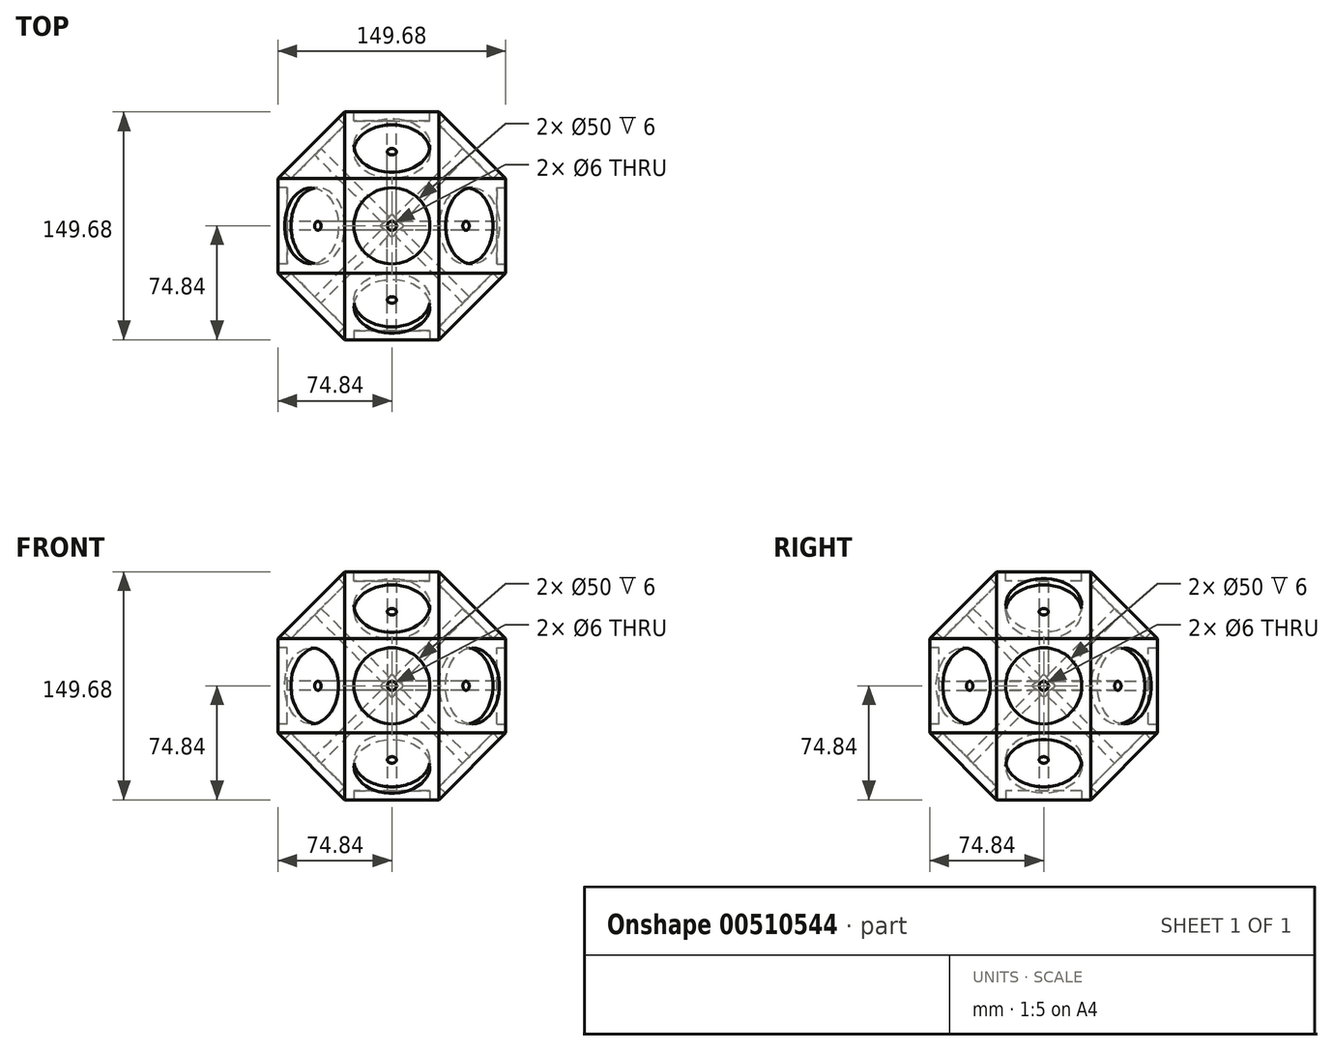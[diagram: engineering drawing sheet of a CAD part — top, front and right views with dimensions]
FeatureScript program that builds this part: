
annotation { "Feature Type Name" : "Feature", "Feature Type Description" : "" }
export const myFeature = defineFeature(function(context is Context, id is Id, definition is map)
    precondition{}
    {
        {
            var Q0;
            Q0=qCreatedBy(makeId("Front.planeOp"),FACE);
            var sketch = newSketch(context, id + "F0", { "sketchPlane" : qUnion([Q0])});
            skLineSegment(sketch, "E0.bottom", {"start": v(0, 0) * mm, "end": v(74.84, 0) * mm, "construction": true});
            skLineSegment(sketch, "E0.top", {"start": v(0, 31) * mm, "end": v(74.84, 31) * mm});
            skLineSegment(sketch, "E0.left", {"start": v(0, 0) * mm, "end": v(0, 31) * mm});
            skLineSegment(sketch, "E0.right", {"start": v(74.84, 0) * mm, "end": v(74.84, 31) * mm});
            skLineSegment(sketch, "E1.top", {"start": v(0, -31) * mm, "end": v(74.84, -31) * mm});
            skLineSegment(sketch, "E1.left", {"start": v(0, 0) * mm, "end": v(0, -31) * mm});
            skLineSegment(sketch, "E1.right", {"start": v(74.84, 0) * mm, "end": v(74.84, -31) * mm});
            skLineSegment(sketch, "E2.bottom", {"start": v(0, 31) * mm, "end": v(-31, 31) * mm, "construction": true});
            skLineSegment(sketch, "E2.top", {"start": v(0, -31) * mm, "end": v(-31, -31) * mm, "construction": true});
            skLineSegment(sketch, "E2.left", {"start": v(0, 31) * mm, "end": v(0, -31) * mm, "construction": true});
            skLineSegment(sketch, "E2.right", {"start": v(-31, 31) * mm, "end": v(-31, -31) * mm, "construction": true});
            skLineSegment(sketch, "E3.bottom", {"start": v(0, 0) * mm, "end": v(31, 0) * mm, "construction": true});
            skLineSegment(sketch, "E3.top", {"start": v(0, 74.84) * mm, "end": v(31, 74.84) * mm, "construction": true});
            skLineSegment(sketch, "E3.left", {"start": v(0, 0) * mm, "end": v(0, 74.84) * mm, "construction": true});
            skLineSegment(sketch, "E3.right", {"start": v(31, 0) * mm, "end": v(31, 74.84) * mm, "construction": true});
            skLineSegment(sketch, "E4.bottom", {"start": v(0, 0) * mm, "end": v(-31, 0) * mm, "construction": true});
            skLineSegment(sketch, "E4.top", {"start": v(0, 74.84) * mm, "end": v(-31, 74.84) * mm, "construction": true});
            skLineSegment(sketch, "E4.right", {"start": v(-31, 0) * mm, "end": v(-31, 74.84) * mm, "construction": true});
            skLineSegment(sketch, "E5", {"start": v(31, 74.84) * mm, "end": v(74.84, 31) * mm, "construction": true});
            skSolve(sketch);
        }
        {
            var Q0;
            Q0=makeQuery(id+"F0.imprint","IMPRINT",FACE,{"disambiguationData":[TD([[makeQuery(id+"F0.imprint","IMPRINT",EDGE,{"derivedFrom":sQuery(id+"F0.wireOp",EDGE,"E0.top")}),-1.0]])]});
            extrude(context, id + "F1", {"entities" : qUnion([Q0]), "depth" : 31 * mm, "hasSecondDirection" : true, "secondDirectionOppositeDirection" : true, "secondDirectionDepth" : 31 * mm});
        }
        {
            var Q0;
            Q0=makeQuery(id+"F1.opExtrude","SWEPT_FACE",FACE,{"disambiguationData":[OSD([sQuery(id+"F0.wireOp",EDGE,"E0.right"),sQuery(id+"F0.wireOp",EDGE,"E1.right")])]});
            var sketch = newSketch(context, id + "F2", { "sketchPlane" : qUnion([Q0])});
            skCircle(sketch, "E6", {"center": v(0, 0) * mm, "radius": 25 * mm});
            skLineSegment(sketch, "E7", {"start": v(0, 0) * mm, "end": v(0, 25) * mm, "construction": true});
            skCircle(sketch, "E8", {"center": v(0, 0) * mm, "radius": 3 * mm});
            skLineSegment(sketch, "E9", {"start": v(0, 0) * mm, "end": v(0, -3) * mm, "construction": true});
            skSolve(sketch);
        }
        {
            var Q0;
            Q0=makeQuery(id+"F2.imprint","IMPRINT",FACE,{"disambiguationData":[TD([[makeQuery(id+"F2.imprint","IMPRINT",EDGE,{"derivedFrom":sQuery(id+"F2.wireOp",EDGE,"E6")}),1.0]])]});
            extrude(context, id + "F3", {"entities" : qUnion([Q0]), "operationType" : NewBodyOperationType.REMOVE, "oppositeDirection" : true, "depth" : 6 * mm});
        }
        {
            var Q0;
            Q0=makeQuery(id+"F1.opExtrude","SWEPT_BODY",BODY,{"disambiguationData":[OSD([sQuery(id+"F0.wireOp",EDGE,"E0.top"),sQuery(id+"F0.wireOp",EDGE,"E0.left"),sQuery(id+"F0.wireOp",EDGE,"E0.right"),sQuery(id+"F0.wireOp",EDGE,"E1.top"),sQuery(id+"F0.wireOp",EDGE,"E1.left"),sQuery(id+"F0.wireOp",EDGE,"E1.right")])]});
            var Q1;
            Q1=sQuery(id+"F0.wireOp",EDGE,"E0.left");
            circularPattern(context, id + "F4", {"operationType" : NewBodyOperationType.ADD, "entities" : qUnion([Q0]), "axis" : qUnion([Q1]), "angle" : 360 * degree, "instanceCount" : 8, "equalSpace" : true});
        }
        {
            var Q0;
            Q0=makeQuery(id+"F1.opExtrude","SWEPT_BODY",BODY,{"disambiguationData":[OSD([sQuery(id+"F0.wireOp",EDGE,"E0.top"),sQuery(id+"F0.wireOp",EDGE,"E0.left"),sQuery(id+"F0.wireOp",EDGE,"E0.right"),sQuery(id+"F0.wireOp",EDGE,"E1.top"),sQuery(id+"F0.wireOp",EDGE,"E1.left"),sQuery(id+"F0.wireOp",EDGE,"E1.right")])]});
            var Q1;
            Q1=sQuery(id+"F0.wireOp",EDGE,"E3.bottom");
            circularPattern(context, id + "F5", {"operationType" : NewBodyOperationType.ADD, "entities" : qUnion([Q0]), "axis" : qUnion([Q1]), "angle" : 90 * degree, "instanceCount" : 2, "equalSpace" : true});
        }
        {
            var Q0;
            Q0=makeQuery(id+"F1.opExtrude","SWEPT_BODY",BODY,{"disambiguationData":[OSD([sQuery(id+"F0.wireOp",EDGE,"E0.top"),sQuery(id+"F0.wireOp",EDGE,"E0.left"),sQuery(id+"F0.wireOp",EDGE,"E0.right"),sQuery(id+"F0.wireOp",EDGE,"E1.top"),sQuery(id+"F0.wireOp",EDGE,"E1.left"),sQuery(id+"F0.wireOp",EDGE,"E1.right")])]});
            var Q1;
            Q1=sQuery(id+"F0.wireOp",EDGE,"E0.left");
            circularPattern(context, id + "F6", {"operationType" : NewBodyOperationType.ADD, "entities" : qUnion([Q0]), "axis" : qUnion([Q1]), "angle" : 90 * degree, "instanceCount" : 2, "equalSpace" : true});
        }
        {
            var Q0;
            Q0=makeQuery(id+"F4.opPattern","COPY",FACE,{"derivedFrom":makeQuery(id+"F3.boolean.opBoolean","SPLIT",FACE,{"disambiguationData":[TD([makeQuery(id+"F3.opExtrude","SWEPT_FACE",FACE,{"disambiguationData":[OSD([sQuery(id+"F2.wireOp",EDGE,"E8")])]})])],"derivedFrom":makeQuery(id+"F1.opExtrude","SWEPT_FACE",FACE,{"disambiguationData":[OSD([sQuery(id+"F0.wireOp",EDGE,"E0.right"),sQuery(id+"F0.wireOp",EDGE,"E1.right")])]})}),"instanceName":"5"});
            extrude(context, id + "F7", {"entities" : qUnion([Q0]), "operationType" : NewBodyOperationType.REMOVE, "endBound" : BoundingType.THROUGH_ALL, "oppositeDirection" : true, "depth" : 25 * mm});
        }
        {
            var Q0;
            Q0=makeQuery(id+"F4.opPattern","COPY",FACE,{"derivedFrom":makeQuery(id+"F3.boolean.opBoolean","SPLIT",FACE,{"disambiguationData":[TD([makeQuery(id+"F3.opExtrude","SWEPT_FACE",FACE,{"disambiguationData":[OSD([sQuery(id+"F2.wireOp",EDGE,"E8")])]})])],"derivedFrom":makeQuery(id+"F1.opExtrude","SWEPT_FACE",FACE,{"disambiguationData":[OSD([sQuery(id+"F0.wireOp",EDGE,"E0.right"),sQuery(id+"F0.wireOp",EDGE,"E1.right")])]})}),"instanceName":"2"});
            extrude(context, id + "F8", {"entities" : qUnion([Q0]), "operationType" : NewBodyOperationType.REMOVE, "endBound" : BoundingType.THROUGH_ALL, "oppositeDirection" : true, "depth" : 25 * mm});
        }
        {
            var Q0;
            Q0=makeQuery(id+"F4.opPattern","COPY",FACE,{"derivedFrom":makeQuery(id+"F3.boolean.opBoolean","SPLIT",FACE,{"disambiguationData":[TD([makeQuery(id+"F3.opExtrude","SWEPT_FACE",FACE,{"disambiguationData":[OSD([sQuery(id+"F2.wireOp",EDGE,"E8")])]})])],"derivedFrom":makeQuery(id+"F1.opExtrude","SWEPT_FACE",FACE,{"disambiguationData":[OSD([sQuery(id+"F0.wireOp",EDGE,"E0.right"),sQuery(id+"F0.wireOp",EDGE,"E1.right")])]})}),"instanceName":"3"});
            extrude(context, id + "F9", {"entities" : qUnion([Q0]), "operationType" : NewBodyOperationType.REMOVE, "endBound" : BoundingType.THROUGH_ALL, "oppositeDirection" : true, "depth" : 25 * mm});
        }
        {
            var Q0;
            Q0=makeQuery(id+"F4.opPattern","COPY",FACE,{"derivedFrom":makeQuery(id+"F3.boolean.opBoolean","SPLIT",FACE,{"disambiguationData":[TD([makeQuery(id+"F3.opExtrude","SWEPT_FACE",FACE,{"disambiguationData":[OSD([sQuery(id+"F2.wireOp",EDGE,"E8")])]})])],"derivedFrom":makeQuery(id+"F1.opExtrude","SWEPT_FACE",FACE,{"disambiguationData":[OSD([sQuery(id+"F0.wireOp",EDGE,"E0.right"),sQuery(id+"F0.wireOp",EDGE,"E1.right")])]})}),"instanceName":"4"});
            extrude(context, id + "F10", {"entities" : qUnion([Q0]), "operationType" : NewBodyOperationType.REMOVE, "endBound" : BoundingType.THROUGH_ALL, "oppositeDirection" : true, "depth" : 25 * mm});
        }
        {
            var Q0;
            Q0=makeQuery(id+"F5.opPattern","COPY",FACE,{"derivedFrom":makeQuery(id+"F4.opPattern","COPY",FACE,{"derivedFrom":makeQuery(id+"F3.boolean.opBoolean","SPLIT",FACE,{"disambiguationData":[TD([makeQuery(id+"F3.opExtrude","SWEPT_FACE",FACE,{"disambiguationData":[OSD([sQuery(id+"F2.wireOp",EDGE,"E8")])]})])],"derivedFrom":makeQuery(id+"F1.opExtrude","SWEPT_FACE",FACE,{"disambiguationData":[OSD([sQuery(id+"F0.wireOp",EDGE,"E0.right"),sQuery(id+"F0.wireOp",EDGE,"E1.right")])]})}),"instanceName":"5"}),"instanceName":"1"});
            extrude(context, id + "F11", {"entities" : qUnion([Q0]), "operationType" : NewBodyOperationType.REMOVE, "endBound" : BoundingType.THROUGH_ALL, "oppositeDirection" : true, "depth" : 25 * mm});
        }
        {
            var Q0;
            Q0=makeQuery(id+"F5.opPattern","COPY",FACE,{"derivedFrom":makeQuery(id+"F4.opPattern","COPY",FACE,{"derivedFrom":makeQuery(id+"F3.boolean.opBoolean","SPLIT",FACE,{"disambiguationData":[TD([makeQuery(id+"F3.opExtrude","SWEPT_FACE",FACE,{"disambiguationData":[OSD([sQuery(id+"F2.wireOp",EDGE,"E8")])]})])],"derivedFrom":makeQuery(id+"F1.opExtrude","SWEPT_FACE",FACE,{"disambiguationData":[OSD([sQuery(id+"F0.wireOp",EDGE,"E0.right"),sQuery(id+"F0.wireOp",EDGE,"E1.right")])]})}),"instanceName":"6"}),"instanceName":"1"});
            extrude(context, id + "F12", {"entities" : qUnion([Q0]), "operationType" : NewBodyOperationType.REMOVE, "endBound" : BoundingType.THROUGH_ALL, "oppositeDirection" : true, "depth" : 25 * mm});
        }
        {
            var Q0;
            Q0=makeQuery(id+"F5.opPattern","COPY",FACE,{"derivedFrom":makeQuery(id+"F4.opPattern","COPY",FACE,{"derivedFrom":makeQuery(id+"F3.boolean.opBoolean","SPLIT",FACE,{"disambiguationData":[TD([makeQuery(id+"F3.opExtrude","SWEPT_FACE",FACE,{"disambiguationData":[OSD([sQuery(id+"F2.wireOp",EDGE,"E8")])]})])],"derivedFrom":makeQuery(id+"F1.opExtrude","SWEPT_FACE",FACE,{"disambiguationData":[OSD([sQuery(id+"F0.wireOp",EDGE,"E0.right"),sQuery(id+"F0.wireOp",EDGE,"E1.right")])]})}),"instanceName":"7"}),"instanceName":"1"});
            extrude(context, id + "F13", {"entities" : qUnion([Q0]), "operationType" : NewBodyOperationType.REMOVE, "endBound" : BoundingType.THROUGH_ALL, "oppositeDirection" : true, "depth" : 25 * mm});
        }
        {
            var Q0;
            Q0=makeQuery(id+"F6.opPattern","COPY",FACE,{"derivedFrom":makeQuery(id+"F5.opPattern","COPY",FACE,{"derivedFrom":makeQuery(id+"F4.opPattern","COPY",FACE,{"derivedFrom":makeQuery(id+"F3.boolean.opBoolean","SPLIT",FACE,{"disambiguationData":[TD([makeQuery(id+"F3.opExtrude","SWEPT_FACE",FACE,{"disambiguationData":[OSD([sQuery(id+"F2.wireOp",EDGE,"E8")])]})])],"derivedFrom":makeQuery(id+"F1.opExtrude","SWEPT_FACE",FACE,{"disambiguationData":[OSD([sQuery(id+"F0.wireOp",EDGE,"E0.right"),sQuery(id+"F0.wireOp",EDGE,"E1.right")])]})}),"instanceName":"7"}),"instanceName":"1"}),"instanceName":"1"});
            extrude(context, id + "F14", {"entities" : qUnion([Q0]), "operationType" : NewBodyOperationType.REMOVE, "endBound" : BoundingType.THROUGH_ALL, "oppositeDirection" : true, "depth" : 25 * mm});
        }
        {
            var Q0;
            Q0=makeQuery(id+"F6.opPattern","COPY",FACE,{"derivedFrom":makeQuery(id+"F5.opPattern","COPY",FACE,{"derivedFrom":makeQuery(id+"F4.opPattern","COPY",FACE,{"derivedFrom":makeQuery(id+"F3.boolean.opBoolean","SPLIT",FACE,{"disambiguationData":[TD([makeQuery(id+"F3.opExtrude","SWEPT_FACE",FACE,{"disambiguationData":[OSD([sQuery(id+"F2.wireOp",EDGE,"E8")])]})])],"derivedFrom":makeQuery(id+"F1.opExtrude","SWEPT_FACE",FACE,{"disambiguationData":[OSD([sQuery(id+"F0.wireOp",EDGE,"E0.right"),sQuery(id+"F0.wireOp",EDGE,"E1.right")])]})}),"instanceName":"1"}),"instanceName":"1"}),"instanceName":"1"});
            extrude(context, id + "F15", {"entities" : qUnion([Q0]), "operationType" : NewBodyOperationType.REMOVE, "endBound" : BoundingType.THROUGH_ALL, "oppositeDirection" : true, "depth" : 25 * mm});
        }
    });
